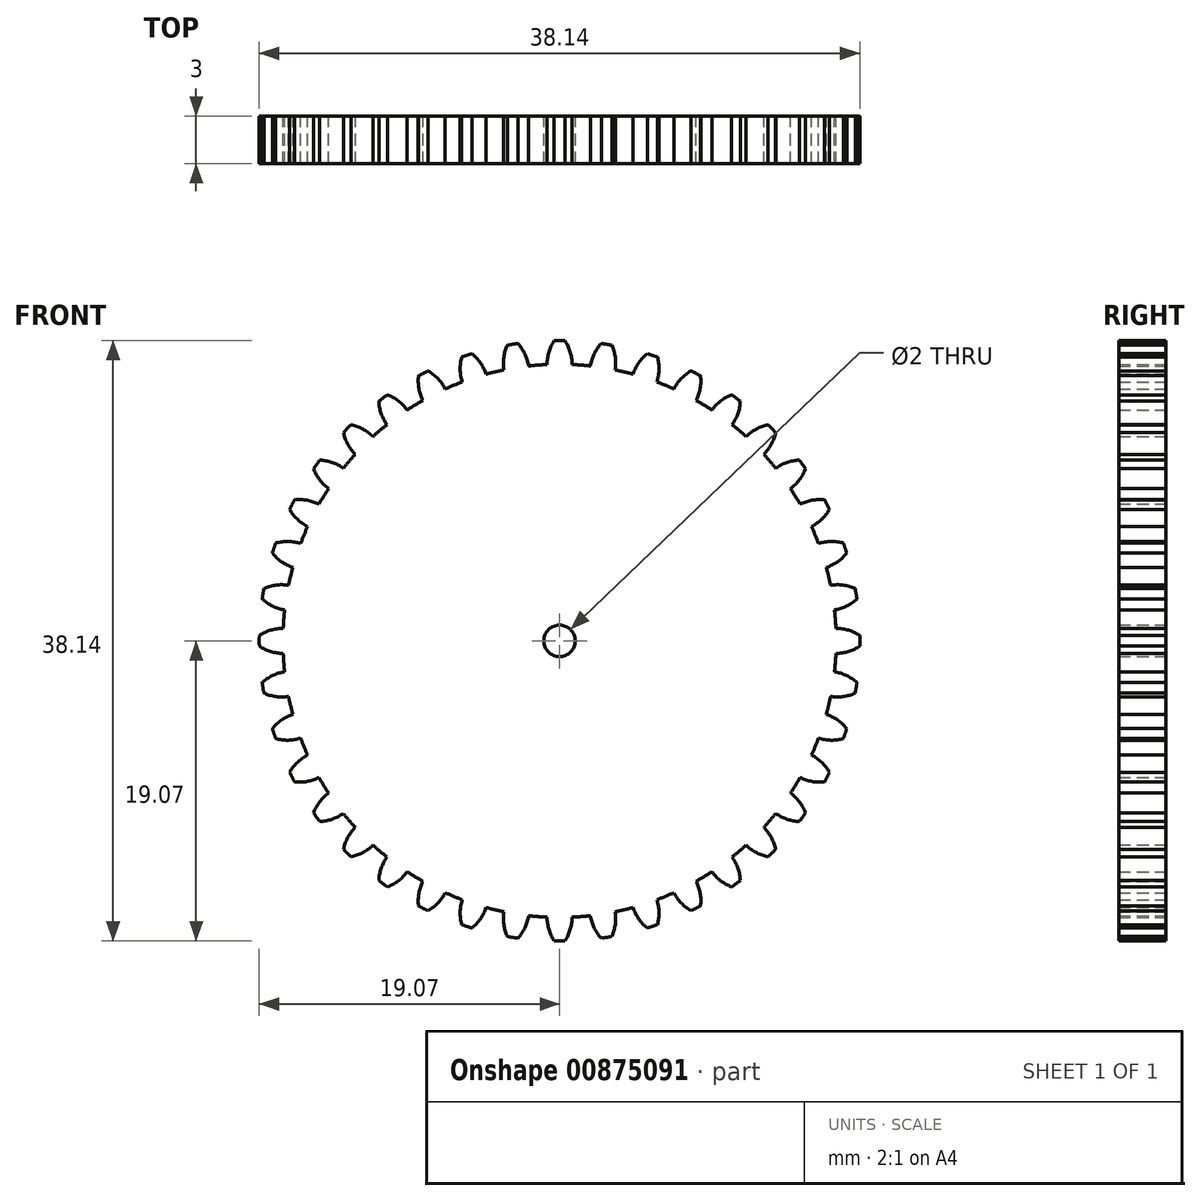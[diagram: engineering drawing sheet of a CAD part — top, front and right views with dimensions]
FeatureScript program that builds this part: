
annotation { "Feature Type Name" : "Feature", "Feature Type Description" : "" }
export const myFeature = defineFeature(function(context is Context, id is Id, definition is map)
    precondition{}
    {
        {
            var Q0;
            Q0=qCreatedBy(makeId("Front.planeOp"),FACE);
            var sketch = newSketch(context, id + "F0", { "sketchPlane" : qUnion([Q0])});
            skCircle(sketch, "E0", {"center": v(0, 0) * mm, "radius": 17.57 * mm});
            skArc(sketch, "E1", {"start": v(0.34, 19.07) * mm, "mid": v(0, 19.07) * mm, "end": v(-0.34, 19.07) * mm});
            skArc(sketch, "E2", {"start": v(-0.34, 19.07) * mm, "mid": v(-0.68, 18.34) * mm, "end": v(-0.8, 17.55) * mm});
            skArc(sketch, "E3.MirrorCS", {"start": v(0.34, 19.07) * mm, "mid": v(0.68, 18.34) * mm, "end": v(0.8, 17.55) * mm});
            skArc(sketch, "E4.1.0", {"start": v(-2.65, 18.89) * mm, "mid": v(-2.2, 18.22) * mm, "end": v(-1.96, 17.46) * mm});
            skArc(sketch, "E4.1.1", {"start": v(-2.65, 18.89) * mm, "mid": v(-2.98, 18.84) * mm, "end": v(-3.32, 18.78) * mm});
            skArc(sketch, "E4.1.2", {"start": v(-3.32, 18.78) * mm, "mid": v(-3.54, 18.01) * mm, "end": v(-3.53, 17.21) * mm});
            skArc(sketch, "E4.2.0", {"start": v(-5.57, 18.24) * mm, "mid": v(-5.02, 17.65) * mm, "end": v(-4.67, 16.94) * mm});
            skArc(sketch, "E4.2.1", {"start": v(-5.57, 18.24) * mm, "mid": v(-5.9, 18.14) * mm, "end": v(-6.21, 18.03) * mm});
            skArc(sketch, "E4.2.2", {"start": v(-6.21, 18.03) * mm, "mid": v(-6.31, 17.24) * mm, "end": v(-6.18, 16.45) * mm});
            skArc(sketch, "E4.3.0", {"start": v(-8.36, 17.14) * mm, "mid": v(-7.72, 16.65) * mm, "end": v(-7.26, 16) * mm});
            skArc(sketch, "E4.3.1", {"start": v(-8.36, 17.14) * mm, "mid": v(-8.66, 17) * mm, "end": v(-8.96, 16.84) * mm});
            skArc(sketch, "E4.3.2", {"start": v(-8.96, 16.84) * mm, "mid": v(-8.93, 16.04) * mm, "end": v(-8.68, 15.28) * mm});
            skArc(sketch, "E4.4.0", {"start": v(-10.93, 15.62) * mm, "mid": v(-10.23, 15.24) * mm, "end": v(-9.67, 14.67) * mm});
            skArc(sketch, "E4.4.1", {"start": v(-10.93, 15.62) * mm, "mid": v(-11.2, 15.43) * mm, "end": v(-11.48, 15.23) * mm});
            skArc(sketch, "E4.4.2", {"start": v(-11.48, 15.23) * mm, "mid": v(-11.33, 14.44) * mm, "end": v(-10.96, 13.73) * mm});
            skArc(sketch, "E4.5.0", {"start": v(-13.24, 13.72) * mm, "mid": v(-12.5, 13.45) * mm, "end": v(-11.85, 12.97) * mm});
            skArc(sketch, "E4.5.1", {"start": v(-13.24, 13.72) * mm, "mid": v(-13.48, 13.48) * mm, "end": v(-13.72, 13.24) * mm});
            skArc(sketch, "E4.5.2", {"start": v(-13.72, 13.24) * mm, "mid": v(-13.45, 12.5) * mm, "end": v(-12.97, 11.85) * mm});
            skArc(sketch, "E4.6.0", {"start": v(-15.23, 11.48) * mm, "mid": v(-14.44, 11.33) * mm, "end": v(-13.73, 10.96) * mm});
            skArc(sketch, "E4.6.1", {"start": v(-15.23, 11.48) * mm, "mid": v(-15.43, 11.2) * mm, "end": v(-15.62, 10.93) * mm});
            skArc(sketch, "E4.6.2", {"start": v(-15.62, 10.93) * mm, "mid": v(-15.24, 10.23) * mm, "end": v(-14.67, 9.67) * mm});
            skArc(sketch, "E4.7.0", {"start": v(-16.84, 8.96) * mm, "mid": v(-16.04, 8.93) * mm, "end": v(-15.28, 8.68) * mm});
            skArc(sketch, "E4.7.1", {"start": v(-16.84, 8.96) * mm, "mid": v(-17, 8.66) * mm, "end": v(-17.14, 8.36) * mm});
            skArc(sketch, "E4.7.2", {"start": v(-17.14, 8.36) * mm, "mid": v(-16.65, 7.72) * mm, "end": v(-16, 7.26) * mm});
            skArc(sketch, "E4.8.0", {"start": v(-18.03, 6.21) * mm, "mid": v(-17.24, 6.31) * mm, "end": v(-16.45, 6.18) * mm});
            skArc(sketch, "E4.8.1", {"start": v(-18.03, 6.21) * mm, "mid": v(-18.14, 5.9) * mm, "end": v(-18.24, 5.57) * mm});
            skArc(sketch, "E4.8.2", {"start": v(-18.24, 5.57) * mm, "mid": v(-17.65, 5.02) * mm, "end": v(-16.94, 4.67) * mm});
            skArc(sketch, "E5.1.9.0", {"start": v(-18.78, 3.32) * mm, "mid": v(-18.01, 3.54) * mm, "end": v(-17.21, 3.53) * mm});
            skArc(sketch, "E5.4.9.0", {"start": v(-18.78, 3.32) * mm, "mid": v(-18.84, 2.98) * mm, "end": v(-18.89, 2.65) * mm});
            skArc(sketch, "E5.8.9.0", {"start": v(-18.89, 2.65) * mm, "mid": v(-18.22, 2.2) * mm, "end": v(-17.46, 1.96) * mm});
            skArc(sketch, "E5.1.10.0", {"start": v(-19.07, 0.34) * mm, "mid": v(-18.34, 0.68) * mm, "end": v(-17.55, 0.8) * mm});
            skArc(sketch, "E5.4.10.0", {"start": v(-19.07, 0.34) * mm, "mid": v(-19.07, 0) * mm, "end": v(-19.07, -0.34) * mm});
            skArc(sketch, "E5.8.10.0", {"start": v(-19.07, -0.34) * mm, "mid": v(-18.34, -0.68) * mm, "end": v(-17.55, -0.8) * mm});
            skArc(sketch, "E5.1.11.0", {"start": v(-18.89, -2.65) * mm, "mid": v(-18.22, -2.2) * mm, "end": v(-17.46, -1.96) * mm});
            skArc(sketch, "E5.4.11.0", {"start": v(-18.89, -2.65) * mm, "mid": v(-18.84, -2.98) * mm, "end": v(-18.78, -3.32) * mm});
            skArc(sketch, "E5.8.11.0", {"start": v(-18.78, -3.32) * mm, "mid": v(-18.01, -3.54) * mm, "end": v(-17.21, -3.53) * mm});
            skArc(sketch, "E5.1.12.0", {"start": v(-18.24, -5.57) * mm, "mid": v(-17.65, -5.02) * mm, "end": v(-16.94, -4.67) * mm});
            skArc(sketch, "E5.4.12.0", {"start": v(-18.24, -5.57) * mm, "mid": v(-18.14, -5.9) * mm, "end": v(-18.03, -6.21) * mm});
            skArc(sketch, "E5.8.12.0", {"start": v(-18.03, -6.21) * mm, "mid": v(-17.24, -6.31) * mm, "end": v(-16.45, -6.18) * mm});
            skArc(sketch, "E5.1.13.0", {"start": v(-17.14, -8.36) * mm, "mid": v(-16.65, -7.72) * mm, "end": v(-16, -7.26) * mm});
            skArc(sketch, "E5.4.13.0", {"start": v(-17.14, -8.36) * mm, "mid": v(-17, -8.66) * mm, "end": v(-16.84, -8.96) * mm});
            skArc(sketch, "E5.8.13.0", {"start": v(-16.84, -8.96) * mm, "mid": v(-16.04, -8.93) * mm, "end": v(-15.28, -8.68) * mm});
            skArc(sketch, "E5.1.14.0", {"start": v(-15.62, -10.93) * mm, "mid": v(-15.24, -10.23) * mm, "end": v(-14.67, -9.67) * mm});
            skArc(sketch, "E5.4.14.0", {"start": v(-15.62, -10.93) * mm, "mid": v(-15.43, -11.2) * mm, "end": v(-15.23, -11.48) * mm});
            skArc(sketch, "E5.8.14.0", {"start": v(-15.23, -11.48) * mm, "mid": v(-14.44, -11.33) * mm, "end": v(-13.73, -10.96) * mm});
            skArc(sketch, "E5.1.15.0", {"start": v(-13.72, -13.24) * mm, "mid": v(-13.45, -12.5) * mm, "end": v(-12.97, -11.85) * mm});
            skArc(sketch, "E5.4.15.0", {"start": v(-13.72, -13.24) * mm, "mid": v(-13.48, -13.48) * mm, "end": v(-13.24, -13.72) * mm});
            skArc(sketch, "E5.8.15.0", {"start": v(-13.24, -13.72) * mm, "mid": v(-12.5, -13.45) * mm, "end": v(-11.85, -12.97) * mm});
            skArc(sketch, "E5.1.16.0", {"start": v(-11.48, -15.23) * mm, "mid": v(-11.33, -14.44) * mm, "end": v(-10.96, -13.73) * mm});
            skArc(sketch, "E5.4.16.0", {"start": v(-11.48, -15.23) * mm, "mid": v(-11.2, -15.43) * mm, "end": v(-10.93, -15.62) * mm});
            skArc(sketch, "E5.8.16.0", {"start": v(-10.93, -15.62) * mm, "mid": v(-10.23, -15.24) * mm, "end": v(-9.67, -14.67) * mm});
            skArc(sketch, "E5.1.17.0", {"start": v(-8.96, -16.84) * mm, "mid": v(-8.93, -16.04) * mm, "end": v(-8.68, -15.28) * mm});
            skArc(sketch, "E5.4.17.0", {"start": v(-8.96, -16.84) * mm, "mid": v(-8.66, -17) * mm, "end": v(-8.36, -17.14) * mm});
            skArc(sketch, "E5.8.17.0", {"start": v(-8.36, -17.14) * mm, "mid": v(-7.72, -16.65) * mm, "end": v(-7.26, -16) * mm});
            skArc(sketch, "E6.1.18.0", {"start": v(-6.21, -18.03) * mm, "mid": v(-6.31, -17.24) * mm, "end": v(-6.18, -16.45) * mm});
            skArc(sketch, "E6.4.18.0", {"start": v(-6.21, -18.03) * mm, "mid": v(-5.9, -18.14) * mm, "end": v(-5.57, -18.24) * mm});
            skArc(sketch, "E6.8.18.0", {"start": v(-5.57, -18.24) * mm, "mid": v(-5.02, -17.65) * mm, "end": v(-4.67, -16.94) * mm});
            skArc(sketch, "E7.1.19.0", {"start": v(-3.32, -18.78) * mm, "mid": v(-3.54, -18.01) * mm, "end": v(-3.53, -17.21) * mm});
            skArc(sketch, "E7.4.19.0", {"start": v(-3.32, -18.78) * mm, "mid": v(-2.98, -18.84) * mm, "end": v(-2.65, -18.89) * mm});
            skArc(sketch, "E7.8.19.0", {"start": v(-2.65, -18.89) * mm, "mid": v(-2.2, -18.22) * mm, "end": v(-1.96, -17.46) * mm});
            skArc(sketch, "E8.1.20.0", {"start": v(-0.34, -19.07) * mm, "mid": v(-0.68, -18.34) * mm, "end": v(-0.8, -17.55) * mm});
            skArc(sketch, "E8.4.20.0", {"start": v(-0.34, -19.07) * mm, "mid": v(0, -19.07) * mm, "end": v(0.34, -19.07) * mm});
            skArc(sketch, "E8.8.20.0", {"start": v(0.34, -19.07) * mm, "mid": v(0.68, -18.34) * mm, "end": v(0.8, -17.55) * mm});
            skArc(sketch, "E8.1.21.0", {"start": v(2.65, -18.89) * mm, "mid": v(2.2, -18.22) * mm, "end": v(1.96, -17.46) * mm});
            skArc(sketch, "E8.4.21.0", {"start": v(2.65, -18.89) * mm, "mid": v(2.98, -18.84) * mm, "end": v(3.32, -18.78) * mm});
            skArc(sketch, "E8.8.21.0", {"start": v(3.32, -18.78) * mm, "mid": v(3.54, -18.01) * mm, "end": v(3.53, -17.21) * mm});
            skArc(sketch, "E8.1.22.0", {"start": v(5.57, -18.24) * mm, "mid": v(5.02, -17.65) * mm, "end": v(4.67, -16.94) * mm});
            skArc(sketch, "E8.4.22.0", {"start": v(5.57, -18.24) * mm, "mid": v(5.9, -18.14) * mm, "end": v(6.21, -18.03) * mm});
            skArc(sketch, "E8.8.22.0", {"start": v(6.21, -18.03) * mm, "mid": v(6.31, -17.24) * mm, "end": v(6.18, -16.45) * mm});
            skArc(sketch, "E8.1.23.0", {"start": v(8.36, -17.14) * mm, "mid": v(7.72, -16.65) * mm, "end": v(7.26, -16) * mm});
            skArc(sketch, "E8.4.23.0", {"start": v(8.36, -17.14) * mm, "mid": v(8.66, -17) * mm, "end": v(8.96, -16.84) * mm});
            skArc(sketch, "E8.8.23.0", {"start": v(8.96, -16.84) * mm, "mid": v(8.93, -16.04) * mm, "end": v(8.68, -15.28) * mm});
            skArc(sketch, "E8.1.24.0", {"start": v(10.93, -15.62) * mm, "mid": v(10.23, -15.24) * mm, "end": v(9.67, -14.67) * mm});
            skArc(sketch, "E8.4.24.0", {"start": v(10.93, -15.62) * mm, "mid": v(11.2, -15.43) * mm, "end": v(11.48, -15.23) * mm});
            skArc(sketch, "E8.8.24.0", {"start": v(11.48, -15.23) * mm, "mid": v(11.33, -14.44) * mm, "end": v(10.96, -13.73) * mm});
            skArc(sketch, "E8.1.25.0", {"start": v(13.24, -13.72) * mm, "mid": v(12.5, -13.45) * mm, "end": v(11.85, -12.97) * mm});
            skArc(sketch, "E8.4.25.0", {"start": v(13.24, -13.72) * mm, "mid": v(13.48, -13.48) * mm, "end": v(13.72, -13.24) * mm});
            skArc(sketch, "E8.8.25.0", {"start": v(13.72, -13.24) * mm, "mid": v(13.45, -12.5) * mm, "end": v(12.97, -11.85) * mm});
            skArc(sketch, "E8.1.26.0", {"start": v(15.23, -11.48) * mm, "mid": v(14.44, -11.33) * mm, "end": v(13.73, -10.96) * mm});
            skArc(sketch, "E8.4.26.0", {"start": v(15.23, -11.48) * mm, "mid": v(15.43, -11.2) * mm, "end": v(15.62, -10.93) * mm});
            skArc(sketch, "E8.8.26.0", {"start": v(15.62, -10.93) * mm, "mid": v(15.24, -10.23) * mm, "end": v(14.67, -9.67) * mm});
            skArc(sketch, "E8.1.27.0", {"start": v(16.84, -8.96) * mm, "mid": v(16.04, -8.93) * mm, "end": v(15.28, -8.68) * mm});
            skArc(sketch, "E8.4.27.0", {"start": v(16.84, -8.96) * mm, "mid": v(17, -8.66) * mm, "end": v(17.14, -8.36) * mm});
            skArc(sketch, "E8.8.27.0", {"start": v(17.14, -8.36) * mm, "mid": v(16.65, -7.72) * mm, "end": v(16, -7.26) * mm});
            skArc(sketch, "E8.1.28.0", {"start": v(18.03, -6.21) * mm, "mid": v(17.24, -6.31) * mm, "end": v(16.45, -6.18) * mm});
            skArc(sketch, "E8.4.28.0", {"start": v(18.03, -6.21) * mm, "mid": v(18.14, -5.9) * mm, "end": v(18.24, -5.57) * mm});
            skArc(sketch, "E8.8.28.0", {"start": v(18.24, -5.57) * mm, "mid": v(17.65, -5.02) * mm, "end": v(16.94, -4.67) * mm});
            skArc(sketch, "E8.1.29.0", {"start": v(18.78, -3.32) * mm, "mid": v(18.01, -3.54) * mm, "end": v(17.21, -3.53) * mm});
            skArc(sketch, "E8.4.29.0", {"start": v(18.78, -3.32) * mm, "mid": v(18.84, -2.98) * mm, "end": v(18.89, -2.65) * mm});
            skArc(sketch, "E8.8.29.0", {"start": v(18.89, -2.65) * mm, "mid": v(18.22, -2.2) * mm, "end": v(17.46, -1.96) * mm});
            skArc(sketch, "E9.1.30.0", {"start": v(19.07, -0.34) * mm, "mid": v(18.34, -0.68) * mm, "end": v(17.55, -0.8) * mm});
            skArc(sketch, "E9.4.30.0", {"start": v(19.07, -0.34) * mm, "mid": v(19.07, 0) * mm, "end": v(19.07, 0.34) * mm});
            skArc(sketch, "E9.8.30.0", {"start": v(19.07, 0.34) * mm, "mid": v(18.34, 0.68) * mm, "end": v(17.55, 0.8) * mm});
            skArc(sketch, "E9.1.31.0", {"start": v(18.89, 2.65) * mm, "mid": v(18.22, 2.2) * mm, "end": v(17.46, 1.96) * mm});
            skArc(sketch, "E9.4.31.0", {"start": v(18.89, 2.65) * mm, "mid": v(18.84, 2.98) * mm, "end": v(18.78, 3.32) * mm});
            skArc(sketch, "E9.8.31.0", {"start": v(18.78, 3.32) * mm, "mid": v(18.01, 3.54) * mm, "end": v(17.21, 3.53) * mm});
            skArc(sketch, "E9.1.32.0", {"start": v(18.24, 5.57) * mm, "mid": v(17.65, 5.02) * mm, "end": v(16.94, 4.67) * mm});
            skArc(sketch, "E9.4.32.0", {"start": v(18.24, 5.57) * mm, "mid": v(18.14, 5.9) * mm, "end": v(18.03, 6.21) * mm});
            skArc(sketch, "E9.8.32.0", {"start": v(18.03, 6.21) * mm, "mid": v(17.24, 6.31) * mm, "end": v(16.45, 6.18) * mm});
            skArc(sketch, "E9.1.33.0", {"start": v(17.14, 8.36) * mm, "mid": v(16.65, 7.72) * mm, "end": v(16, 7.26) * mm});
            skArc(sketch, "E9.4.33.0", {"start": v(17.14, 8.36) * mm, "mid": v(17, 8.66) * mm, "end": v(16.84, 8.96) * mm});
            skArc(sketch, "E9.8.33.0", {"start": v(16.84, 8.96) * mm, "mid": v(16.04, 8.93) * mm, "end": v(15.28, 8.68) * mm});
            skArc(sketch, "E9.1.34.0", {"start": v(15.62, 10.93) * mm, "mid": v(15.24, 10.23) * mm, "end": v(14.67, 9.67) * mm});
            skArc(sketch, "E9.4.34.0", {"start": v(15.62, 10.93) * mm, "mid": v(15.43, 11.2) * mm, "end": v(15.23, 11.48) * mm});
            skArc(sketch, "E9.8.34.0", {"start": v(15.23, 11.48) * mm, "mid": v(14.44, 11.33) * mm, "end": v(13.73, 10.96) * mm});
            skArc(sketch, "E9.1.35.0", {"start": v(13.72, 13.24) * mm, "mid": v(13.45, 12.5) * mm, "end": v(12.97, 11.85) * mm});
            skArc(sketch, "E9.4.35.0", {"start": v(13.72, 13.24) * mm, "mid": v(13.48, 13.48) * mm, "end": v(13.24, 13.72) * mm});
            skArc(sketch, "E9.8.35.0", {"start": v(13.24, 13.72) * mm, "mid": v(12.5, 13.45) * mm, "end": v(11.85, 12.97) * mm});
            skArc(sketch, "E9.1.36.0", {"start": v(11.48, 15.23) * mm, "mid": v(11.33, 14.44) * mm, "end": v(10.96, 13.73) * mm});
            skArc(sketch, "E9.4.36.0", {"start": v(11.48, 15.23) * mm, "mid": v(11.2, 15.43) * mm, "end": v(10.93, 15.62) * mm});
            skArc(sketch, "E9.8.36.0", {"start": v(10.93, 15.62) * mm, "mid": v(10.23, 15.24) * mm, "end": v(9.67, 14.67) * mm});
            skArc(sketch, "E9.1.37.0", {"start": v(8.96, 16.84) * mm, "mid": v(8.93, 16.04) * mm, "end": v(8.68, 15.28) * mm});
            skArc(sketch, "E9.4.37.0", {"start": v(8.96, 16.84) * mm, "mid": v(8.66, 17) * mm, "end": v(8.36, 17.14) * mm});
            skArc(sketch, "E9.8.37.0", {"start": v(8.36, 17.14) * mm, "mid": v(7.72, 16.65) * mm, "end": v(7.26, 16) * mm});
            skArc(sketch, "E9.1.38.0", {"start": v(6.21, 18.03) * mm, "mid": v(6.31, 17.24) * mm, "end": v(6.18, 16.45) * mm});
            skArc(sketch, "E9.4.38.0", {"start": v(6.21, 18.03) * mm, "mid": v(5.9, 18.14) * mm, "end": v(5.57, 18.24) * mm});
            skArc(sketch, "E9.8.38.0", {"start": v(5.57, 18.24) * mm, "mid": v(5.02, 17.65) * mm, "end": v(4.67, 16.94) * mm});
            skArc(sketch, "E9.1.39.0", {"start": v(3.32, 18.78) * mm, "mid": v(3.54, 18.01) * mm, "end": v(3.53, 17.21) * mm});
            skArc(sketch, "E9.4.39.0", {"start": v(3.32, 18.78) * mm, "mid": v(2.98, 18.84) * mm, "end": v(2.65, 18.89) * mm});
            skArc(sketch, "E9.8.39.0", {"start": v(2.65, 18.89) * mm, "mid": v(2.2, 18.22) * mm, "end": v(1.96, 17.46) * mm});
            skSolve(sketch);
        }
        {
            var Q0;
            Q0=qSketchRegion(id+"F0",true);
            extrude(context, id + "F1", {"entities" : qUnion([Q0]), "depth" : 3 * mm, "offsetDistance" : 25 * mm});
        }
        {
            var Q0;
            Q0=makeQuery(id+"F1.opExtrude","CAP_FACE",FACE,{"disambiguationData":[OSD([sQuery(id+"F0.wireOp",EDGE,"E0"),sQuery(id+"F0.wireOp",EDGE,"E1"),sQuery(id+"F0.wireOp",EDGE,"E2"),sQuery(id+"F0.wireOp",EDGE,"E3.MirrorCS"),sQuery(id+"F0.wireOp",EDGE,"E4.1.0"),sQuery(id+"F0.wireOp",EDGE,"E4.1.1"),sQuery(id+"F0.wireOp",EDGE,"E4.1.2"),sQuery(id+"F0.wireOp",EDGE,"E4.2.0"),sQuery(id+"F0.wireOp",EDGE,"E4.2.1"),sQuery(id+"F0.wireOp",EDGE,"E4.2.2"),sQuery(id+"F0.wireOp",EDGE,"E4.3.0"),sQuery(id+"F0.wireOp",EDGE,"E4.3.1"),sQuery(id+"F0.wireOp",EDGE,"E4.3.2"),sQuery(id+"F0.wireOp",EDGE,"E4.4.0"),sQuery(id+"F0.wireOp",EDGE,"E4.4.1"),sQuery(id+"F0.wireOp",EDGE,"E4.4.2"),sQuery(id+"F0.wireOp",EDGE,"E4.5.0"),sQuery(id+"F0.wireOp",EDGE,"E4.5.1"),sQuery(id+"F0.wireOp",EDGE,"E4.5.2"),sQuery(id+"F0.wireOp",EDGE,"E4.6.0"),sQuery(id+"F0.wireOp",EDGE,"E4.6.1"),sQuery(id+"F0.wireOp",EDGE,"E4.6.2"),sQuery(id+"F0.wireOp",EDGE,"E4.7.0"),sQuery(id+"F0.wireOp",EDGE,"E4.7.1"),sQuery(id+"F0.wireOp",EDGE,"E4.7.2"),sQuery(id+"F0.wireOp",EDGE,"E4.8.0"),sQuery(id+"F0.wireOp",EDGE,"E4.8.1"),sQuery(id+"F0.wireOp",EDGE,"E4.8.2")])],"isStart":true});
            var sketch = newSketch(context, id + "F2", { "sketchPlane" : qUnion([Q0])});
            skCircle(sketch, "E10", {"center": v(0, 0) * mm, "radius": 1 * mm});
            skSolve(sketch);
        }
        {
            var Q0;
            Q0=makeQuery(id+"F2.imprint","IMPRINT",FACE,{"disambiguationData":[TD([[makeQuery(id+"F2.imprint","IMPRINT",EDGE,{"derivedFrom":sQuery(id+"F2.wireOp",EDGE,"E10")}),1.0]])]});
            extrude(context, id + "F3", {"entities" : qUnion([Q0]), "operationType" : NewBodyOperationType.REMOVE, "endBound" : BoundingType.THROUGH_ALL, "oppositeDirection" : true, "depth" : 25 * mm, "offsetDistance" : 25 * mm});
        }
        {
            var Q0;
            Q0=makeQuery(id+"F1.opExtrude","SWEPT_BODY",BODY,{"disambiguationData":[OSD([sQuery(id+"F0.wireOp",EDGE,"E0"),sQuery(id+"F0.wireOp",EDGE,"E1"),sQuery(id+"F0.wireOp",EDGE,"E2"),sQuery(id+"F0.wireOp",EDGE,"E3.MirrorCS"),sQuery(id+"F0.wireOp",EDGE,"E4.1.0"),sQuery(id+"F0.wireOp",EDGE,"E4.1.1"),sQuery(id+"F0.wireOp",EDGE,"E4.1.2"),sQuery(id+"F0.wireOp",EDGE,"E4.2.0"),sQuery(id+"F0.wireOp",EDGE,"E4.2.1"),sQuery(id+"F0.wireOp",EDGE,"E4.2.2"),sQuery(id+"F0.wireOp",EDGE,"E4.3.0"),sQuery(id+"F0.wireOp",EDGE,"E4.3.1"),sQuery(id+"F0.wireOp",EDGE,"E4.3.2"),sQuery(id+"F0.wireOp",EDGE,"E4.4.0"),sQuery(id+"F0.wireOp",EDGE,"E4.4.1"),sQuery(id+"F0.wireOp",EDGE,"E4.4.2"),sQuery(id+"F0.wireOp",EDGE,"E4.5.0"),sQuery(id+"F0.wireOp",EDGE,"E4.5.1"),sQuery(id+"F0.wireOp",EDGE,"E4.5.2"),sQuery(id+"F0.wireOp",EDGE,"E4.6.0"),sQuery(id+"F0.wireOp",EDGE,"E4.6.1"),sQuery(id+"F0.wireOp",EDGE,"E4.6.2"),sQuery(id+"F0.wireOp",EDGE,"E4.7.0"),sQuery(id+"F0.wireOp",EDGE,"E4.7.1"),sQuery(id+"F0.wireOp",EDGE,"E4.7.2"),sQuery(id+"F0.wireOp",EDGE,"E4.8.0"),sQuery(id+"F0.wireOp",EDGE,"E4.8.1"),sQuery(id+"F0.wireOp",EDGE,"E4.8.2")])]});
            transform(context, id + "F4", {"entities" : qUnion([Q0]), "transformType" : TransformType.TRANSLATION_3D, "dx" : 0 * mm, "dy" : 0 * mm, "dz" : 0 * mm, "makeCopy" : true});
        }
        {
            var Q0;
            Q0=makeQuery(id+"F4.opPattern","COPY",BODY,{"derivedFrom":makeQuery(id+"F1.opExtrude","SWEPT_BODY",BODY,{"disambiguationData":[OSD([sQuery(id+"F0.wireOp",EDGE,"E0"),sQuery(id+"F0.wireOp",EDGE,"E1"),sQuery(id+"F0.wireOp",EDGE,"E2"),sQuery(id+"F0.wireOp",EDGE,"E3.MirrorCS"),sQuery(id+"F0.wireOp",EDGE,"E4.1.0"),sQuery(id+"F0.wireOp",EDGE,"E4.1.1"),sQuery(id+"F0.wireOp",EDGE,"E4.1.2"),sQuery(id+"F0.wireOp",EDGE,"E4.2.0"),sQuery(id+"F0.wireOp",EDGE,"E4.2.1"),sQuery(id+"F0.wireOp",EDGE,"E4.2.2"),sQuery(id+"F0.wireOp",EDGE,"E4.3.0"),sQuery(id+"F0.wireOp",EDGE,"E4.3.1"),sQuery(id+"F0.wireOp",EDGE,"E4.3.2"),sQuery(id+"F0.wireOp",EDGE,"E4.4.0"),sQuery(id+"F0.wireOp",EDGE,"E4.4.1"),sQuery(id+"F0.wireOp",EDGE,"E4.4.2"),sQuery(id+"F0.wireOp",EDGE,"E4.5.0"),sQuery(id+"F0.wireOp",EDGE,"E4.5.1"),sQuery(id+"F0.wireOp",EDGE,"E4.5.2"),sQuery(id+"F0.wireOp",EDGE,"E4.6.0"),sQuery(id+"F0.wireOp",EDGE,"E4.6.1"),sQuery(id+"F0.wireOp",EDGE,"E4.6.2"),sQuery(id+"F0.wireOp",EDGE,"E4.7.0"),sQuery(id+"F0.wireOp",EDGE,"E4.7.1"),sQuery(id+"F0.wireOp",EDGE,"E4.7.2"),sQuery(id+"F0.wireOp",EDGE,"E4.8.0"),sQuery(id+"F0.wireOp",EDGE,"E4.8.1"),sQuery(id+"F0.wireOp",EDGE,"E4.8.2")])]}),"instanceName":"1"});
            deleteBodies(context, id + "F5", {"entities" : qUnion([Q0])});
        }
    });
